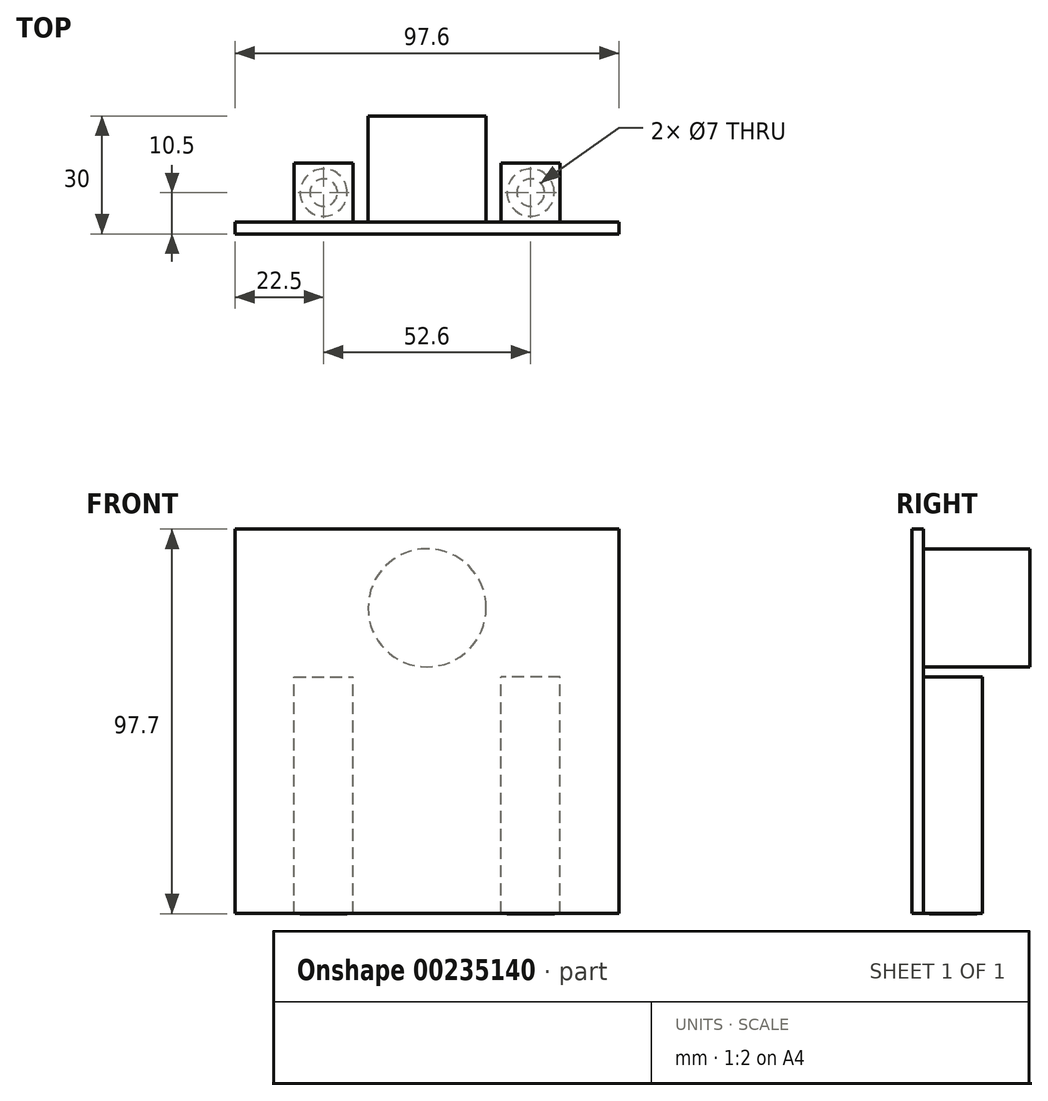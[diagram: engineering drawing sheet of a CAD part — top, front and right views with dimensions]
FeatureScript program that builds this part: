
annotation { "Feature Type Name" : "Feature", "Feature Type Description" : "" }
export const myFeature = defineFeature(function(context is Context, id is Id, definition is map)
    precondition{}
    {
        {
            var Q0;
            Q0=qCreatedBy(makeId("Front.planeOp"),FACE);
            var sketch = newSketch(context, id + "F0", { "sketchPlane" : qUnion([Q0])});
            skLineSegment(sketch, "E0.bottom", {"start": v(0, 0) * mm, "end": v(97.6, 0) * mm});
            skLineSegment(sketch, "E0.top", {"start": v(0, 97.6) * mm, "end": v(97.6, 97.6) * mm});
            skLineSegment(sketch, "E0.left", {"start": v(0, 0) * mm, "end": v(0, 97.6) * mm});
            skLineSegment(sketch, "E0.right", {"start": v(97.6, 0) * mm, "end": v(97.6, 97.6) * mm});
            skSolve(sketch);
        }
        {
            var Q0;
            Q0 = qSketchRegion(id + "F0", true);
            extrude(context, id + "F1", {"entities" : qUnion([Q0]), "depth" : 3 * mm});
        }
        {
            var Q0;
            Q0=makeQuery(id+"F1.opExtrude","CAP_FACE",FACE,{"disambiguationData":[OSD([sQuery(id+"F0.wireOp",EDGE,"E0.bottom"),sQuery(id+"F0.wireOp",EDGE,"E0.top"),sQuery(id+"F0.wireOp",EDGE,"E0.left"),sQuery(id+"F0.wireOp",EDGE,"E0.right")])],"isStart":true});
            var sketch = newSketch(context, id + "F2", { "sketchPlane" : qUnion([Q0])});
            skLineSegment(sketch, "E1.bottom", {"start": v(-15, 0) * mm, "end": v(-30, 0) * mm});
            skLineSegment(sketch, "E1.top", {"start": v(-15, 60) * mm, "end": v(-30, 60) * mm});
            skLineSegment(sketch, "E1.left", {"start": v(-15, 0) * mm, "end": v(-15, 60) * mm});
            skLineSegment(sketch, "E1.right", {"start": v(-30, 0) * mm, "end": v(-30, 60) * mm});
            skLineSegment(sketch, "E2", {"start": v(-48.8, 97.6) * mm, "end": v(-48.8, 0) * mm, "construction": true});
            skLineSegment(sketch, "E3.MirrorCS", {"start": v(-82.6, 0) * mm, "end": v(-82.6, 60) * mm});
            skLineSegment(sketch, "E4.MirrorCS", {"start": v(-82.6, 60) * mm, "end": v(-67.6, 60) * mm});
            skLineSegment(sketch, "E5.MirrorCS", {"start": v(-67.6, 0) * mm, "end": v(-67.6, 60) * mm});
            skLineSegment(sketch, "E6.MirrorCS", {"start": v(-82.6, 0) * mm, "end": v(-67.6, 0) * mm});
            skSolve(sketch);
        }
        {
            var Q0;
            Q0 = qSketchRegion(id + "F2", true);
            extrude(context, id + "F3", {"entities" : qUnion([Q0]), "depth" : 15 * mm});
        }
        {
            var Q0;
            Q0=makeQuery(id+"F3.opExtrude","SWEPT_FACE",FACE,{"disambiguationData":[OSD([sQuery(id+"F2.wireOp",EDGE,"E1.bottom")])]});
            var sketch = newSketch(context, id + "F4", { "sketchPlane" : qUnion([Q0])});
            skCircle(sketch, "E7", {"center": v(22.5, -7.5) * mm, "radius": 6 * mm});
            skCircle(sketch, "E8", {"center": v(22.5, -7.5) * mm, "radius": 3.5 * mm});
            skSolve(sketch);
        }
        {
            var Q0;
            Q0 = qSketchRegion(id + "F4", true);
            extrude(context, id + "F5", {"entities" : qUnion([Q0]), "depth" : 0.1 * mm});
        }
        {
            var Q0;
            Q0=makeQuery(id+"F3.opExtrude","SWEPT_FACE",FACE,{"disambiguationData":[OSD([sQuery(id+"F2.wireOp",EDGE,"E6.MirrorCS")])]});
            var sketch = newSketch(context, id + "F6", { "sketchPlane" : qUnion([Q0])});
            skCircle(sketch, "E9", {"center": v(75.1, -7.5) * mm, "radius": 6 * mm});
            skCircle(sketch, "E10", {"center": v(75.1, -7.5) * mm, "radius": 3.5 * mm});
            skSolve(sketch);
        }
        {
            var Q0;
            Q0 = qSketchRegion(id + "F6", true);
            extrude(context, id + "F7", {"entities" : qUnion([Q0]), "depth" : 0.1 * mm});
        }
        {
            var Q0;
            Q0=makeQuery(id+"F3.opExtrude","SWEPT_FACE",FACE,{"disambiguationData":[OSD([sQuery(id+"F2.wireOp",EDGE,"E6.MirrorCS")])]});
            var sketch = newSketch(context, id + "F8", { "sketchPlane" : qUnion([Q0])});
            skCircle(sketch, "E11", {"center": v(75.1, -7.5) * mm, "radius": 3.5 * mm});
            skSolve(sketch);
        }
        {
            var Q0;
            Q0 = qSketchRegion(id + "F8", true);
            extrude(context, id + "F9", {"entities" : qUnion([Q0]), "depth" : 0.1 * mm});
        }
        {
            var Q0;
            Q0=makeQuery(id+"F3.opExtrude","SWEPT_FACE",FACE,{"disambiguationData":[OSD([sQuery(id+"F2.wireOp",EDGE,"E1.bottom")])]});
            var sketch = newSketch(context, id + "F10", { "sketchPlane" : qUnion([Q0])});
            skCircle(sketch, "E12", {"center": v(22.5, -7.5) * mm, "radius": 3.5 * mm});
            skSolve(sketch);
        }
        {
            var Q0;
            Q0=makeQuery(id+"F10.imprint","IMPRINT",FACE,{"disambiguationData":[TD([[makeQuery(id+"F10.imprint","IMPRINT",EDGE,{"derivedFrom":sQuery(id+"F10.wireOp",EDGE,"E12")}),1.0]])]});
            extrude(context, id + "F11", {"entities" : qUnion([Q0]), "depth" : 0.1 * mm});
        }
        {
            var Q0;
            Q0=makeQuery(id+"F1.opExtrude","CAP_FACE",FACE,{"disambiguationData":[OSD([sQuery(id+"F0.wireOp",EDGE,"E0.bottom"),sQuery(id+"F0.wireOp",EDGE,"E0.top"),sQuery(id+"F0.wireOp",EDGE,"E0.left"),sQuery(id+"F0.wireOp",EDGE,"E0.right")])],"isStart":true});
            var sketch = newSketch(context, id + "F12", { "sketchPlane" : qUnion([Q0])});
            skCircle(sketch, "E13", {"center": v(-48.8, 77.6) * mm, "radius": 15 * mm});
            skSolve(sketch);
        }
        {
            var Q0;
            Q0=makeQuery(id+"F12.imprint","IMPRINT",FACE,{"disambiguationData":[TD([[makeQuery(id+"F12.imprint","IMPRINT",EDGE,{"derivedFrom":sQuery(id+"F12.wireOp",EDGE,"E13")}),1.0]])]});
            extrude(context, id + "F13", {"entities" : qUnion([Q0]), "depth" : 27 * mm});
        }
    });
